# Revit family: 2-HC_RAC_HCL_TOSHIBA_TCTC_PKVPG_10-16
name_source: partatom
category: Generic Models
revit_build: Autodesk Revit 2017 (Build: 20160225_1515(x64)
units: mm (PartAtom-declared; Revit-internal decimal feet)

## family parameters
Always vertical = Yes
Can host rebar = No
Cut with Voids When Loaded = No
Part Type = Normal
Room Calculation Point = No
Round Connector Dimension = Use Diameter
Shared = No
Work Plane-Based = No

## types (6) — shared parameters
Compressor detail (Motor output kW) = -
Compressor detail (Type) = -
Content Supplier URL = www.hcltech.com
Custom = Yes
Depth (mm) = 270 mm  [stored 0.885827 ft]
Drain pipe = 16 mm  [stored 0.0524934 ft]
Duct diameter (mm) = -
EMCS = 4
ETIM Article Class = EC001213
Frequency (Hz) = 50Hz
Height (mm) = 293 mm  [stored 0.961286 ft]
MCA (A) = -
MEPcontent Class = HEATPUMP
Manufacturer = "Toshiba"
Manufacturer URL = https://www.toshiba-carrier.co.jp
Operating range degC-Cooling = 21 - 32
Operating range degC-Heating = 0 - 28
Piping diameter Liquid (mm) = 6 mm  [stored 0.019685 ft]
Power consumption-Cooling (Kw) = 25
Power consumption-Heating (Kw) = 30
Product Line = TCTC
Red = Colour RGB-250 000 000
Refrigerant information = R32
Revit Version = 2017
Running current-Cooling (A) = 0.24 - 0.22
Running current-Heating (A) = 0.28 - 0.26
Static pressure = -
URL = https://www.toshiba-carrier.co.jp
Voltage (V) = 220-240V
Weight (Kg) = 14 mm  [stored 0.0459318 ft]
White = Colour - RGB 255 255 255
Width (mm) = 851 mm  [stored 2.79199 ft]

## per-type parameters (varying)
| type | Air filter | Airflow m3/h | Article Description | Description | Energy class-Cooling/Heating | MOCP (A) | Pdesigh-Cooling/Heating | Piping diameter Gas (mm) | Rated Capacity kW -Cooling/Heating | Rated Power Consumption kW-Cooling/Heating | Rated efficiency-EER / COP | Seasonal Efficiency-SEER  / SCOP | Sound pressure - Cooling/Heating (dB) High | Sound pressure - Cooling/Heating (dB) Mid | Sound pressure -Cooling/Heating (dB) Low | Sound pressure dB(A)-Cooling/Heating-Low+ | Sound pressure dB(A)-Cooling/Heating-Mid+ | Starting current (A) |
| RAS-10PKVPG-E | Plasma ion charger filtration | 684 / 726 | R32 DSK 9 | R32 DSK 9 | A+++ / A+++ | 15 | 2.5 / 3.0 (Tbiv= -7degC) | 10 mm  [stored 0.0328084 ft] | 2.5 / 3.2 | 0.45 / 0.60 | 5.56 / 5.33 | 10.6 / 5.20 | 43 / 44 | 33 / 33 | 24 / 24 | 28 / 28 | 39 / 39 | - |
| RAS-13PKVPG-E | Long life filter | 714 / 726 | R32 DSK 9 | R32 DSK 9 | A+++ / A+++ | 15 | 3.5 / 3.6 (Tbiv= -7degC) | 10 mm  [stored 0.0328084 ft] | 3.5 / 4.0 | 0.75 / 0.80 | 4.67 / 5.00 | 9.50 / 5.10 | 44 / 45 | 34 / 34 | 25 / 25 | 29 / 29 | 39 / 39 | - |
| RAS-16PKVPG-E | Long life filter | 732 / 744 | R32 DSK 9 | R32 DSK 9 | A+++ / A+++ | 15 | 4.5 / 4.5 (Tbiv= -7degC) | 13 mm  [stored 0.0426509 ft] | 4.5 / 5.5 | 1.08 / 1.37 | 4.17 / 4.01 | 8.50 / 4.60 | 45 / 46 | 35 / 35 | 26 / 26 | 30 / 30 | 40 / 40 | 6.44 - 5.89 |
| RAS-M10PKVPG-E | Plamsa air purifier | 672 / 726 | Hi-wall - Daiseikai 9 | Hi-wall - Daiseikai 9 | - | 10 | - | 10 mm  [stored 0.0328084 ft] | - | - | - | - | 42 / 44 | - | - | - | - | - |
| RAS-M13PKVPG-E | Plamsa air purifier | 672 / 726 | Hi-wall - Daiseikai 9 | Hi-wall - Daiseikai 9 | - | 10 | - | 10 mm  [stored 0.0328084 ft] | - | - | - | - | 43 / 44 | - | - | - | - | - |
| RAS-M16PKVPG-E | Plamsa air purifier | 672 / 744 | Hi-wall - Daiseikai 9 | Hi-wall - Daiseikai 9 | - | - | - | 10 mm  [stored 0.0328084 ft] | - | - | - | - | 44 / 45 | - | - | - | - | - |

note: column(s) folded — value = type name in every type: Article Type, Manufacturer Art. No., Model

note: [stored X ft] marks values corroborated as IEEE doubles in the binary element streams (Revit-internal decimal feet)

## geometry (parser evidence)
native form markers: Sweep x3
no freeform markers — native parametric forms only
